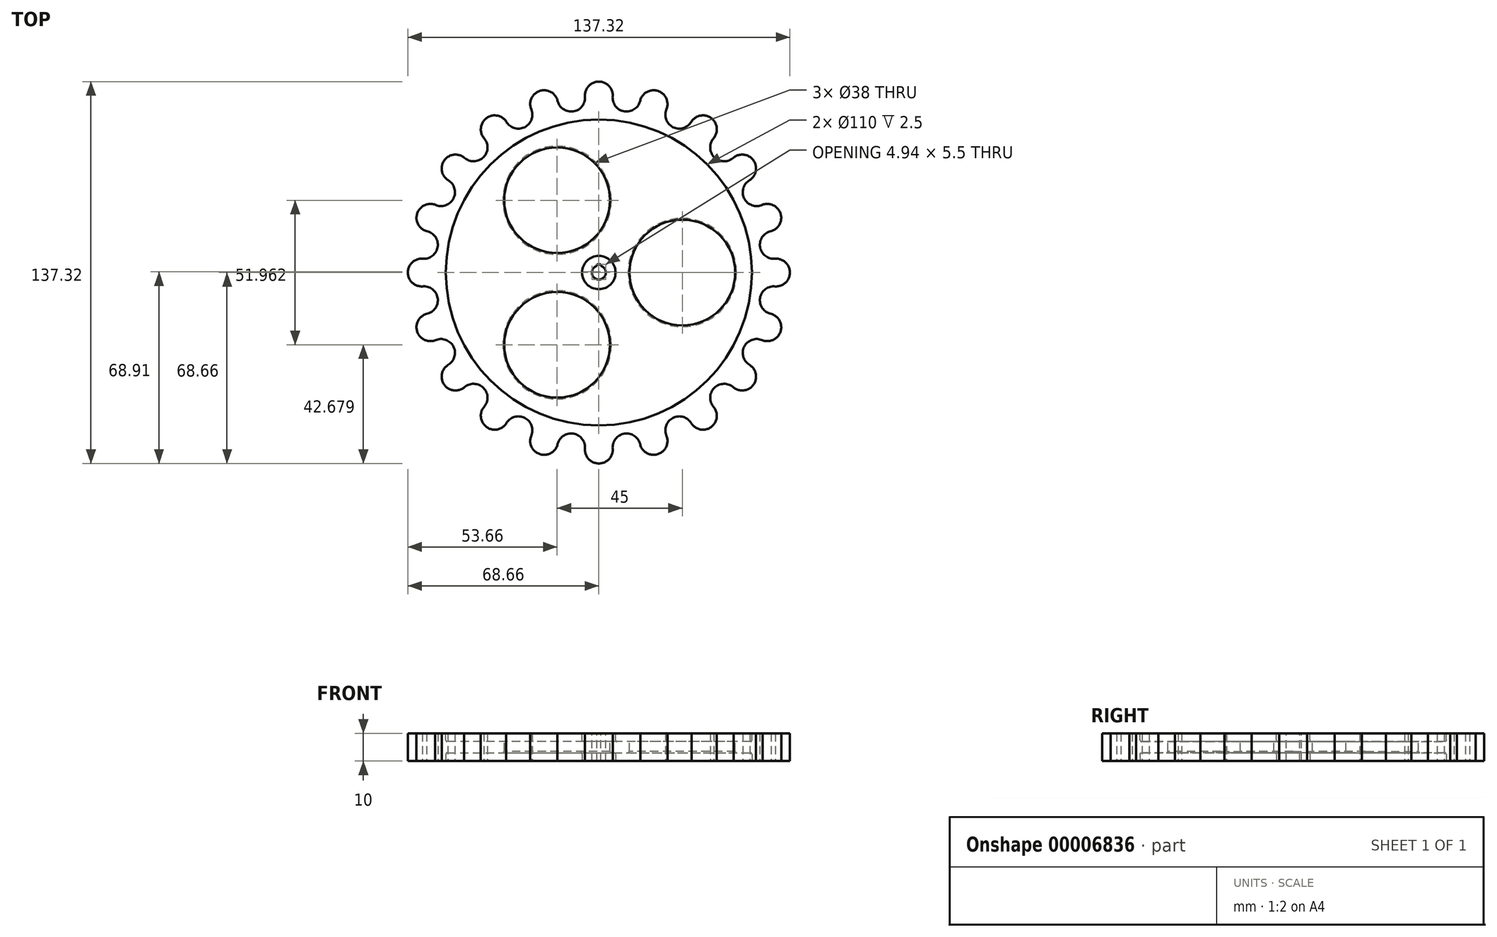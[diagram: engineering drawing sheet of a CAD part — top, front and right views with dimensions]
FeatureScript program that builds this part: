
annotation { "Feature Type Name" : "Feature", "Feature Type Description" : "" }
export const myFeature = defineFeature(function(context is Context, id is Id, definition is map)
    precondition{}
    {
        {
            var Q0;
            Q0=qCreatedBy(makeId("Top.planeOp"),FACE);
            var sketch = newSketch(context, id + "F0", { "sketchPlane" : qUnion([Q0])});
            skArc(sketch, "E0", {"start": v(4.96, 63.04) * mm, "mid": v(0, 68.66) * mm, "end": v(-4.96, 63.04) * mm});
            skCircle(sketch, "E1.1.0", {"center": v(-9.96, 62.88) * mm, "radius": 5 * mm});
            skArc(sketch, "E1.2.0", {"start": v(-14.76, 61.5) * mm, "mid": v(-21.22, 65.3) * mm, "end": v(-24.2, 58.43) * mm});
            skCircle(sketch, "E1.3.0", {"center": v(-28.9, 56.72) * mm, "radius": 5 * mm});
            skArc(sketch, "E1.4.0", {"start": v(-33.04, 53.92) * mm, "mid": v(-40.36, 55.55) * mm, "end": v(-41.07, 48.09) * mm});
            skCircle(sketch, "E1.5.0", {"center": v(-45.02, 45.02) * mm, "radius": 5 * mm});
            skArc(sketch, "E1.6.0", {"start": v(-48.09, 41.07) * mm, "mid": v(-55.55, 40.36) * mm, "end": v(-53.92, 33.04) * mm});
            skCircle(sketch, "E1.7.0", {"center": v(-56.72, 28.9) * mm, "radius": 5 * mm});
            skArc(sketch, "E1.8.0", {"start": v(-58.43, 24.2) * mm, "mid": v(-65.3, 21.22) * mm, "end": v(-61.5, 14.76) * mm});
            skCircle(sketch, "E1.9.0", {"center": v(-62.88, 9.96) * mm, "radius": 5 * mm});
            skArc(sketch, "E1.10.0", {"start": v(-63.04, 4.96) * mm, "mid": v(-68.66, 0) * mm, "end": v(-63.04, -4.96) * mm});
            skCircle(sketch, "E1.11.0", {"center": v(-62.88, -9.96) * mm, "radius": 5 * mm});
            skArc(sketch, "E1.12.0", {"start": v(-61.5, -14.76) * mm, "mid": v(-65.3, -21.22) * mm, "end": v(-58.43, -24.2) * mm});
            skCircle(sketch, "E1.13.0", {"center": v(-56.72, -28.9) * mm, "radius": 5 * mm});
            skArc(sketch, "E1.14.0", {"start": v(-53.92, -33.04) * mm, "mid": v(-55.55, -40.36) * mm, "end": v(-48.09, -41.07) * mm});
            skCircle(sketch, "E1.15.0", {"center": v(-45.02, -45.02) * mm, "radius": 5 * mm});
            skArc(sketch, "E1.16.0", {"start": v(-41.07, -48.09) * mm, "mid": v(-40.36, -55.55) * mm, "end": v(-33.04, -53.92) * mm});
            skCircle(sketch, "E1.17.0", {"center": v(-28.9, -56.72) * mm, "radius": 5 * mm});
            skArc(sketch, "E1.18.0", {"start": v(-24.2, -58.43) * mm, "mid": v(-21.22, -65.3) * mm, "end": v(-14.76, -61.5) * mm});
            skCircle(sketch, "E1.19.0", {"center": v(-9.96, -62.88) * mm, "radius": 5 * mm});
            skArc(sketch, "E1.20.0", {"start": v(-4.96, -63.04) * mm, "mid": v(0, -68.66) * mm, "end": v(4.96, -63.04) * mm});
            skCircle(sketch, "E1.21.0", {"center": v(9.96, -62.88) * mm, "radius": 5 * mm});
            skArc(sketch, "E1.22.0", {"start": v(14.76, -61.5) * mm, "mid": v(21.22, -65.3) * mm, "end": v(24.2, -58.43) * mm});
            skCircle(sketch, "E1.23.0", {"center": v(28.9, -56.72) * mm, "radius": 5 * mm});
            skArc(sketch, "E1.24.0", {"start": v(33.04, -53.92) * mm, "mid": v(40.36, -55.55) * mm, "end": v(41.07, -48.09) * mm});
            skCircle(sketch, "E1.25.0", {"center": v(45.02, -45.02) * mm, "radius": 5 * mm});
            skArc(sketch, "E1.26.0", {"start": v(48.09, -41.07) * mm, "mid": v(55.55, -40.36) * mm, "end": v(53.92, -33.04) * mm});
            skCircle(sketch, "E1.27.0", {"center": v(56.72, -28.9) * mm, "radius": 5 * mm});
            skArc(sketch, "E1.28.0", {"start": v(58.43, -24.2) * mm, "mid": v(65.3, -21.22) * mm, "end": v(61.5, -14.76) * mm});
            skCircle(sketch, "E1.29.0", {"center": v(62.88, -9.96) * mm, "radius": 5 * mm});
            skArc(sketch, "E1.30.0", {"start": v(63.04, -4.96) * mm, "mid": v(68.66, 0) * mm, "end": v(63.04, 4.96) * mm});
            skCircle(sketch, "E1.31.0", {"center": v(62.88, 9.96) * mm, "radius": 5 * mm});
            skArc(sketch, "E1.32.0", {"start": v(61.5, 14.76) * mm, "mid": v(65.3, 21.22) * mm, "end": v(58.43, 24.2) * mm});
            skCircle(sketch, "E1.33.0", {"center": v(56.72, 28.9) * mm, "radius": 5 * mm});
            skArc(sketch, "E1.34.0", {"start": v(53.92, 33.04) * mm, "mid": v(55.55, 40.36) * mm, "end": v(48.09, 41.07) * mm});
            skCircle(sketch, "E1.35.0", {"center": v(45.02, 45.02) * mm, "radius": 5 * mm});
            skArc(sketch, "E1.36.0", {"start": v(41.07, 48.09) * mm, "mid": v(40.36, 55.55) * mm, "end": v(33.04, 53.92) * mm});
            skCircle(sketch, "E1.37.0", {"center": v(28.9, 56.72) * mm, "radius": 5 * mm});
            skArc(sketch, "E1.38.0", {"start": v(24.2, 58.43) * mm, "mid": v(21.22, 65.3) * mm, "end": v(14.76, 61.5) * mm});
            skCircle(sketch, "E1.39.0", {"center": v(9.96, 62.88) * mm, "radius": 5 * mm});
            skPoint(sketch, "E1.center", {"position": v(0, 0) * mm});
            skSolve(sketch);
        }
        {
            var Q0;
            {var subQ0=sQuery(id+"F0.wireOp",EDGE,"E1.39.0");var subQ42=sQuery(id+"F0.wireOp",EDGE,"E0");var subQ81=makeQuery(id+"F0.imprint","INTERSECT",VERTEX,{"disambiguationData":[OD(1.0)],"derivedFrom":[subQ42,subQ0]});Q0=makeQuery(id+"F0.imprint","IMPRINT",FACE,{"disambiguationData":[TD([[makeQuery(id+"F0.imprint","IMPRINT",EDGE,{"disambiguationData":[TD([[subQ81,-1.0]])],"derivedFrom":subQ42}),1.0]])]});}
            extrude(context, id + "F1", {"entities" : qUnion([Q0]), "depth" : 10 * mm});
        }
        {
            var Q0;
            Q0=makeQuery(id+"F1.opExtrude","CAP_FACE",FACE,{"disambiguationData":[OSD([sQuery(id+"F0.wireOp",EDGE,"E0"),sQuery(id+"F0.wireOp",EDGE,"E1.1.0"),sQuery(id+"F0.wireOp",EDGE,"E1.2.0"),sQuery(id+"F0.wireOp",EDGE,"E1.3.0"),sQuery(id+"F0.wireOp",EDGE,"E1.4.0"),sQuery(id+"F0.wireOp",EDGE,"E1.5.0"),sQuery(id+"F0.wireOp",EDGE,"E1.6.0"),sQuery(id+"F0.wireOp",EDGE,"E1.7.0"),sQuery(id+"F0.wireOp",EDGE,"E1.8.0"),sQuery(id+"F0.wireOp",EDGE,"E1.9.0"),sQuery(id+"F0.wireOp",EDGE,"E1.10.0"),sQuery(id+"F0.wireOp",EDGE,"E1.11.0"),sQuery(id+"F0.wireOp",EDGE,"E1.12.0"),sQuery(id+"F0.wireOp",EDGE,"E1.13.0"),sQuery(id+"F0.wireOp",EDGE,"E1.14.0"),sQuery(id+"F0.wireOp",EDGE,"E1.15.0"),sQuery(id+"F0.wireOp",EDGE,"E1.16.0"),sQuery(id+"F0.wireOp",EDGE,"E1.17.0"),sQuery(id+"F0.wireOp",EDGE,"E1.18.0"),sQuery(id+"F0.wireOp",EDGE,"E1.19.0"),sQuery(id+"F0.wireOp",EDGE,"E1.20.0"),sQuery(id+"F0.wireOp",EDGE,"E1.21.0"),sQuery(id+"F0.wireOp",EDGE,"E1.22.0"),sQuery(id+"F0.wireOp",EDGE,"E1.23.0"),sQuery(id+"F0.wireOp",EDGE,"E1.24.0"),sQuery(id+"F0.wireOp",EDGE,"E1.25.0"),sQuery(id+"F0.wireOp",EDGE,"E1.26.0"),sQuery(id+"F0.wireOp",EDGE,"E1.27.0"),sQuery(id+"F0.wireOp",EDGE,"E1.28.0"),sQuery(id+"F0.wireOp",EDGE,"E1.29.0"),sQuery(id+"F0.wireOp",EDGE,"E1.30.0"),sQuery(id+"F0.wireOp",EDGE,"E1.31.0"),sQuery(id+"F0.wireOp",EDGE,"E1.32.0"),sQuery(id+"F0.wireOp",EDGE,"E1.33.0"),sQuery(id+"F0.wireOp",EDGE,"E1.34.0"),sQuery(id+"F0.wireOp",EDGE,"E1.35.0"),sQuery(id+"F0.wireOp",EDGE,"E1.36.0"),sQuery(id+"F0.wireOp",EDGE,"E1.37.0"),sQuery(id+"F0.wireOp",EDGE,"E1.38.0"),sQuery(id+"F0.wireOp",EDGE,"E1.39.0")])],"isStart":false});
            var sketch = newSketch(context, id + "F2", { "sketchPlane" : qUnion([Q0])});
            skArc(sketch, "E2", {"start": v(-0.75, 2.38) * mm, "mid": v(0, -2.5) * mm, "end": v(0.75, 2.38) * mm});
            skLineSegment(sketch, "E3", {"start": v(0, 3) * mm, "end": v(-0.75, 3) * mm});
            skLineSegment(sketch, "E4", {"start": v(-0.75, 3) * mm, "end": v(-0.75, 2.38) * mm});
            skLineSegment(sketch, "E5.0.MirrorCS", {"start": v(0, 3) * mm, "end": v(0.75, 3) * mm});
            skLineSegment(sketch, "E5.1.MirrorCS", {"start": v(0.75, 3) * mm, "end": v(0.75, 2.38) * mm});
            skSolve(sketch);
        }
        {
            var Q0;
            Q0=makeQuery(id+"F2.imprint","IMPRINT",FACE,{"disambiguationData":[TD([[makeQuery(id+"F2.imprint","IMPRINT",EDGE,{"derivedFrom":sQuery(id+"F2.wireOp",EDGE,"E2")}),1.0]])]});
            extrude(context, id + "F3", {"entities" : qUnion([Q0]), "operationType" : NewBodyOperationType.REMOVE, "endBound" : BoundingType.THROUGH_ALL, "oppositeDirection" : true, "depth" : 25 * mm});
        }
        {
            var Q0;
            Q0=makeQuery(id+"F1.opExtrude","CAP_FACE",FACE,{"disambiguationData":[OSD([sQuery(id+"F0.wireOp",EDGE,"E0"),sQuery(id+"F0.wireOp",EDGE,"E1.1.0"),sQuery(id+"F0.wireOp",EDGE,"E1.2.0"),sQuery(id+"F0.wireOp",EDGE,"E1.3.0"),sQuery(id+"F0.wireOp",EDGE,"E1.4.0"),sQuery(id+"F0.wireOp",EDGE,"E1.5.0"),sQuery(id+"F0.wireOp",EDGE,"E1.6.0"),sQuery(id+"F0.wireOp",EDGE,"E1.7.0"),sQuery(id+"F0.wireOp",EDGE,"E1.8.0"),sQuery(id+"F0.wireOp",EDGE,"E1.9.0"),sQuery(id+"F0.wireOp",EDGE,"E1.10.0"),sQuery(id+"F0.wireOp",EDGE,"E1.11.0"),sQuery(id+"F0.wireOp",EDGE,"E1.12.0"),sQuery(id+"F0.wireOp",EDGE,"E1.13.0"),sQuery(id+"F0.wireOp",EDGE,"E1.14.0"),sQuery(id+"F0.wireOp",EDGE,"E1.15.0"),sQuery(id+"F0.wireOp",EDGE,"E1.16.0"),sQuery(id+"F0.wireOp",EDGE,"E1.17.0"),sQuery(id+"F0.wireOp",EDGE,"E1.18.0"),sQuery(id+"F0.wireOp",EDGE,"E1.19.0"),sQuery(id+"F0.wireOp",EDGE,"E1.20.0"),sQuery(id+"F0.wireOp",EDGE,"E1.21.0"),sQuery(id+"F0.wireOp",EDGE,"E1.22.0"),sQuery(id+"F0.wireOp",EDGE,"E1.23.0"),sQuery(id+"F0.wireOp",EDGE,"E1.24.0"),sQuery(id+"F0.wireOp",EDGE,"E1.25.0"),sQuery(id+"F0.wireOp",EDGE,"E1.26.0"),sQuery(id+"F0.wireOp",EDGE,"E1.27.0"),sQuery(id+"F0.wireOp",EDGE,"E1.28.0"),sQuery(id+"F0.wireOp",EDGE,"E1.29.0"),sQuery(id+"F0.wireOp",EDGE,"E1.30.0"),sQuery(id+"F0.wireOp",EDGE,"E1.31.0"),sQuery(id+"F0.wireOp",EDGE,"E1.32.0"),sQuery(id+"F0.wireOp",EDGE,"E1.33.0"),sQuery(id+"F0.wireOp",EDGE,"E1.34.0"),sQuery(id+"F0.wireOp",EDGE,"E1.35.0"),sQuery(id+"F0.wireOp",EDGE,"E1.36.0"),sQuery(id+"F0.wireOp",EDGE,"E1.37.0"),sQuery(id+"F0.wireOp",EDGE,"E1.38.0"),sQuery(id+"F0.wireOp",EDGE,"E1.39.0")])],"isStart":false});
            var sketch = newSketch(context, id + "F4", { "sketchPlane" : qUnion([Q0])});
            skCircle(sketch, "E6", {"center": v(0, 0) * mm, "radius": 6 * mm});
            skCircle(sketch, "E7", {"center": v(0, 0) * mm, "radius": 55 * mm});
            skSolve(sketch);
        }
        {
            var Q0;
            Q0=makeQuery(id+"F4.imprint","IMPRINT",FACE,{"disambiguationData":[TD([[makeQuery(id+"F4.imprint","IMPRINT",EDGE,{"derivedFrom":sQuery(id+"F4.wireOp",EDGE,"E6")}),-1.0]])]});
            extrude(context, id + "F5", {"entities" : qUnion([Q0]), "operationType" : NewBodyOperationType.REMOVE, "oppositeDirection" : true, "depth" : 3 * mm});
        }
        {
            var Q0;
            Q0=makeQuery(id+"F1.opExtrude","CAP_FACE",FACE,{"disambiguationData":[OSD([sQuery(id+"F0.wireOp",EDGE,"E0"),sQuery(id+"F0.wireOp",EDGE,"E1.1.0"),sQuery(id+"F0.wireOp",EDGE,"E1.2.0"),sQuery(id+"F0.wireOp",EDGE,"E1.3.0"),sQuery(id+"F0.wireOp",EDGE,"E1.4.0"),sQuery(id+"F0.wireOp",EDGE,"E1.5.0"),sQuery(id+"F0.wireOp",EDGE,"E1.6.0"),sQuery(id+"F0.wireOp",EDGE,"E1.7.0"),sQuery(id+"F0.wireOp",EDGE,"E1.8.0"),sQuery(id+"F0.wireOp",EDGE,"E1.9.0"),sQuery(id+"F0.wireOp",EDGE,"E1.10.0"),sQuery(id+"F0.wireOp",EDGE,"E1.11.0"),sQuery(id+"F0.wireOp",EDGE,"E1.12.0"),sQuery(id+"F0.wireOp",EDGE,"E1.13.0"),sQuery(id+"F0.wireOp",EDGE,"E1.14.0"),sQuery(id+"F0.wireOp",EDGE,"E1.15.0"),sQuery(id+"F0.wireOp",EDGE,"E1.16.0"),sQuery(id+"F0.wireOp",EDGE,"E1.17.0"),sQuery(id+"F0.wireOp",EDGE,"E1.18.0"),sQuery(id+"F0.wireOp",EDGE,"E1.19.0"),sQuery(id+"F0.wireOp",EDGE,"E1.20.0"),sQuery(id+"F0.wireOp",EDGE,"E1.21.0"),sQuery(id+"F0.wireOp",EDGE,"E1.22.0"),sQuery(id+"F0.wireOp",EDGE,"E1.23.0"),sQuery(id+"F0.wireOp",EDGE,"E1.24.0"),sQuery(id+"F0.wireOp",EDGE,"E1.25.0"),sQuery(id+"F0.wireOp",EDGE,"E1.26.0"),sQuery(id+"F0.wireOp",EDGE,"E1.27.0"),sQuery(id+"F0.wireOp",EDGE,"E1.28.0"),sQuery(id+"F0.wireOp",EDGE,"E1.29.0"),sQuery(id+"F0.wireOp",EDGE,"E1.30.0"),sQuery(id+"F0.wireOp",EDGE,"E1.31.0"),sQuery(id+"F0.wireOp",EDGE,"E1.32.0"),sQuery(id+"F0.wireOp",EDGE,"E1.33.0"),sQuery(id+"F0.wireOp",EDGE,"E1.34.0"),sQuery(id+"F0.wireOp",EDGE,"E1.35.0"),sQuery(id+"F0.wireOp",EDGE,"E1.36.0"),sQuery(id+"F0.wireOp",EDGE,"E1.37.0"),sQuery(id+"F0.wireOp",EDGE,"E1.38.0"),sQuery(id+"F0.wireOp",EDGE,"E1.39.0")])],"isStart":true});
            var sketch = newSketch(context, id + "F6", { "sketchPlane" : qUnion([Q0])});
            skCircle(sketch, "E8", {"center": v(0, 0) * mm, "radius": 6 * mm});
            skCircle(sketch, "E9", {"center": v(0, 0) * mm, "radius": 55 * mm});
            skSolve(sketch);
        }
        {
            var Q0;
            Q0=makeQuery(id+"F6.imprint","IMPRINT",FACE,{"disambiguationData":[TD([[makeQuery(id+"F6.imprint","IMPRINT",EDGE,{"derivedFrom":sQuery(id+"F6.wireOp",EDGE,"E8")}),-1.0]])]});
            extrude(context, id + "F7", {"entities" : qUnion([Q0]), "operationType" : NewBodyOperationType.REMOVE, "oppositeDirection" : true, "depth" : 3 * mm});
        }
        {
            var Q0;
            Q0=makeQuery(id+"F5.boolean.opBoolean","COPY",FACE,{"derivedFrom":makeQuery(id+"F5.opExtrude","CAP_FACE",FACE,{"disambiguationData":[OSD([sQuery(id+"F4.wireOp",EDGE,"E6"),sQuery(id+"F4.wireOp",EDGE,"E7")])],"isStart":false})});
            var sketch = newSketch(context, id + "F8", { "sketchPlane" : qUnion([Q0])});
            skCircle(sketch, "E10", {"center": v(30, 0) * mm, "radius": 19 * mm});
            skCircle(sketch, "E11.1.0", {"center": v(-15, -25.98) * mm, "radius": 19 * mm});
            skCircle(sketch, "E11.2.0", {"center": v(-15, 25.98) * mm, "radius": 19 * mm});
            skPoint(sketch, "E11.center", {"position": v(0, 0) * mm});
            skLineSegment(sketch, "E11.anchor1", {"start": v(0, 0) * mm, "end": v(30, 0) * mm, "construction": true});
            skLineSegment(sketch, "E11.anchor2", {"start": v(0, 0) * mm, "end": v(-15, 25.98) * mm, "construction": true});
            skSolve(sketch);
        }
        {
            var Q0;
            Q0=makeQuery(id+"F8.imprint","IMPRINT",FACE,{"disambiguationData":[TD([[makeQuery(id+"F8.imprint","IMPRINT",EDGE,{"derivedFrom":sQuery(id+"F8.wireOp",EDGE,"E11.2.0")}),1.0]])]});
            var Q1;
            Q1=makeQuery(id+"F8.imprint","IMPRINT",FACE,{"disambiguationData":[TD([[makeQuery(id+"F8.imprint","IMPRINT",EDGE,{"derivedFrom":sQuery(id+"F8.wireOp",EDGE,"E11.1.0")}),1.0]])]});
            var Q2;
            Q2=makeQuery(id+"F8.imprint","IMPRINT",FACE,{"disambiguationData":[TD([[makeQuery(id+"F8.imprint","IMPRINT",EDGE,{"derivedFrom":sQuery(id+"F8.wireOp",EDGE,"E10")}),1.0]])]});
            extrude(context, id + "F9", {"entities" : qUnion([Q0, Q1, Q2]), "operationType" : NewBodyOperationType.REMOVE, "endBound" : BoundingType.THROUGH_ALL, "oppositeDirection" : true, "depth" : 25 * mm});
        }
        {
            var Q0;
            Q0=makeQuery(id+"F9.boolean.opBoolean","COPY",EDGE,{"derivedFrom":makeQuery(id+"F9.opExtrude","CAP_EDGE",EDGE,{"disambiguationData":[OSD([sQuery(id+"F8.wireOp",EDGE,"E11.1.0")])],"isStart":true})});
            var Q1;
            Q1=makeQuery(id+"F9.boolean.opBoolean","INTERSECT",EDGE,{"derivedFrom":[makeQuery(id+"F7.boolean.opBoolean","COPY",FACE,{"derivedFrom":makeQuery(id+"F7.opExtrude","CAP_FACE",FACE,{"disambiguationData":[OSD([sQuery(id+"F6.wireOp",EDGE,"E8"),sQuery(id+"F6.wireOp",EDGE,"E9")])],"isStart":false})}),makeQuery(id+"F9.opExtrude","SWEPT_FACE",FACE,{"disambiguationData":[OSD([sQuery(id+"F8.wireOp",EDGE,"E11.1.0")])]})]});
            var Q2;
            Q2=makeQuery(id+"F9.boolean.opBoolean","INTERSECT",EDGE,{"derivedFrom":[makeQuery(id+"F7.boolean.opBoolean","COPY",FACE,{"derivedFrom":makeQuery(id+"F7.opExtrude","CAP_FACE",FACE,{"disambiguationData":[OSD([sQuery(id+"F6.wireOp",EDGE,"E8"),sQuery(id+"F6.wireOp",EDGE,"E9")])],"isStart":false})}),makeQuery(id+"F9.opExtrude","SWEPT_FACE",FACE,{"disambiguationData":[OSD([sQuery(id+"F8.wireOp",EDGE,"E11.2.0")])]})]});
            var Q3;
            Q3=makeQuery(id+"F9.boolean.opBoolean","COPY",EDGE,{"derivedFrom":makeQuery(id+"F9.opExtrude","CAP_EDGE",EDGE,{"disambiguationData":[OSD([sQuery(id+"F8.wireOp",EDGE,"E11.2.0")])],"isStart":true})});
            var Q4;
            Q4=makeQuery(id+"F9.boolean.opBoolean","INTERSECT",EDGE,{"derivedFrom":[makeQuery(id+"F7.boolean.opBoolean","COPY",FACE,{"derivedFrom":makeQuery(id+"F7.opExtrude","CAP_FACE",FACE,{"disambiguationData":[OSD([sQuery(id+"F6.wireOp",EDGE,"E8"),sQuery(id+"F6.wireOp",EDGE,"E9")])],"isStart":false})}),makeQuery(id+"F9.opExtrude","SWEPT_FACE",FACE,{"disambiguationData":[OSD([sQuery(id+"F8.wireOp",EDGE,"E10")])]})]});
            var Q5;
            Q5=makeQuery(id+"F9.boolean.opBoolean","COPY",EDGE,{"derivedFrom":makeQuery(id+"F9.opExtrude","CAP_EDGE",EDGE,{"disambiguationData":[OSD([sQuery(id+"F8.wireOp",EDGE,"E10")])],"isStart":true})});
            var Q6;
            Q6=makeQuery(id+"F5.boolean.opBoolean","COPY",EDGE,{"derivedFrom":makeQuery(id+"F5.opExtrude","CAP_EDGE",EDGE,{"disambiguationData":[OSD([sQuery(id+"F4.wireOp",EDGE,"E7")])],"isStart":true})});
            var Q7;
            Q7=makeQuery(id+"F7.boolean.opBoolean","COPY",EDGE,{"derivedFrom":makeQuery(id+"F7.opExtrude","CAP_EDGE",EDGE,{"disambiguationData":[OSD([sQuery(id+"F6.wireOp",EDGE,"E9")])],"isStart":true})});
            chamfer(context, id + "F10", {"entities" : qUnion([Q0, Q1, Q2, Q3, Q4, Q5, Q6, Q7]), "width" : .5 * mm, "tangentPropagation" : true});
        }
        {
            var Q0;
            Q0=makeQuery(id+"F7.boolean.opBoolean","COPY",EDGE,{"derivedFrom":makeQuery(id+"F7.opExtrude","CAP_EDGE",EDGE,{"disambiguationData":[OSD([sQuery(id+"F6.wireOp",EDGE,"E9")])],"isStart":false})});
            var Q1;
            Q1=makeQuery(id+"F7.boolean.opBoolean","COPY",EDGE,{"derivedFrom":makeQuery(id+"F7.opExtrude","CAP_EDGE",EDGE,{"disambiguationData":[OSD([sQuery(id+"F6.wireOp",EDGE,"E8")])],"isStart":false})});
            var Q2;
            Q2=makeQuery(id+"F5.boolean.opBoolean","COPY",EDGE,{"derivedFrom":makeQuery(id+"F5.opExtrude","CAP_EDGE",EDGE,{"disambiguationData":[OSD([sQuery(id+"F4.wireOp",EDGE,"E7")])],"isStart":false})});
            var Q3;
            Q3=makeQuery(id+"F5.boolean.opBoolean","COPY",EDGE,{"derivedFrom":makeQuery(id+"F5.opExtrude","CAP_EDGE",EDGE,{"disambiguationData":[OSD([sQuery(id+"F4.wireOp",EDGE,"E6")])],"isStart":false})});
            fillet(context, id + "F11", {"entities" : qUnion([Q0, Q1, Q2, Q3]), "radius" : .5 * mm, "tangentPropagation" : true, "allowEdgeOverflow" : false});
        }
        {
            var Q0;
            Q0=makeQuery(id+"F1.opExtrude","SWEPT_BODY",BODY,{"disambiguationData":[OSD([sQuery(id+"F0.wireOp",EDGE,"E0"),sQuery(id+"F0.wireOp",EDGE,"E1.1.0"),sQuery(id+"F0.wireOp",EDGE,"E1.2.0"),sQuery(id+"F0.wireOp",EDGE,"E1.3.0"),sQuery(id+"F0.wireOp",EDGE,"E1.4.0"),sQuery(id+"F0.wireOp",EDGE,"E1.5.0"),sQuery(id+"F0.wireOp",EDGE,"E1.6.0"),sQuery(id+"F0.wireOp",EDGE,"E1.7.0"),sQuery(id+"F0.wireOp",EDGE,"E1.8.0"),sQuery(id+"F0.wireOp",EDGE,"E1.9.0"),sQuery(id+"F0.wireOp",EDGE,"E1.10.0"),sQuery(id+"F0.wireOp",EDGE,"E1.11.0"),sQuery(id+"F0.wireOp",EDGE,"E1.12.0"),sQuery(id+"F0.wireOp",EDGE,"E1.13.0"),sQuery(id+"F0.wireOp",EDGE,"E1.14.0"),sQuery(id+"F0.wireOp",EDGE,"E1.15.0"),sQuery(id+"F0.wireOp",EDGE,"E1.16.0"),sQuery(id+"F0.wireOp",EDGE,"E1.17.0"),sQuery(id+"F0.wireOp",EDGE,"E1.18.0"),sQuery(id+"F0.wireOp",EDGE,"E1.19.0"),sQuery(id+"F0.wireOp",EDGE,"E1.20.0"),sQuery(id+"F0.wireOp",EDGE,"E1.21.0"),sQuery(id+"F0.wireOp",EDGE,"E1.22.0"),sQuery(id+"F0.wireOp",EDGE,"E1.23.0"),sQuery(id+"F0.wireOp",EDGE,"E1.24.0"),sQuery(id+"F0.wireOp",EDGE,"E1.25.0"),sQuery(id+"F0.wireOp",EDGE,"E1.26.0"),sQuery(id+"F0.wireOp",EDGE,"E1.27.0"),sQuery(id+"F0.wireOp",EDGE,"E1.28.0"),sQuery(id+"F0.wireOp",EDGE,"E1.29.0"),sQuery(id+"F0.wireOp",EDGE,"E1.30.0"),sQuery(id+"F0.wireOp",EDGE,"E1.31.0"),sQuery(id+"F0.wireOp",EDGE,"E1.32.0"),sQuery(id+"F0.wireOp",EDGE,"E1.33.0"),sQuery(id+"F0.wireOp",EDGE,"E1.34.0"),sQuery(id+"F0.wireOp",EDGE,"E1.35.0"),sQuery(id+"F0.wireOp",EDGE,"E1.36.0"),sQuery(id+"F0.wireOp",EDGE,"E1.37.0"),sQuery(id+"F0.wireOp",EDGE,"E1.38.0"),sQuery(id+"F0.wireOp",EDGE,"E1.39.0")])]});
            transform(context, id + "F12", {"entities" : qUnion([Q0]), "transformType" : TransformType.TRANSLATION_3D, "dx" : 0 * mm, "dy" : 200 * mm, "dz" : 0 * mm, "makeCopy" : true});
        }
        {
            var Q0;
            Q0=makeQuery(id+"F12.opPattern","COPY",BODY,{"derivedFrom":makeQuery(id+"F1.opExtrude","SWEPT_BODY",BODY,{"disambiguationData":[OSD([sQuery(id+"F0.wireOp",EDGE,"E0"),sQuery(id+"F0.wireOp",EDGE,"E1.1.0"),sQuery(id+"F0.wireOp",EDGE,"E1.2.0"),sQuery(id+"F0.wireOp",EDGE,"E1.3.0"),sQuery(id+"F0.wireOp",EDGE,"E1.4.0"),sQuery(id+"F0.wireOp",EDGE,"E1.5.0"),sQuery(id+"F0.wireOp",EDGE,"E1.6.0"),sQuery(id+"F0.wireOp",EDGE,"E1.7.0"),sQuery(id+"F0.wireOp",EDGE,"E1.8.0"),sQuery(id+"F0.wireOp",EDGE,"E1.9.0"),sQuery(id+"F0.wireOp",EDGE,"E1.10.0"),sQuery(id+"F0.wireOp",EDGE,"E1.11.0"),sQuery(id+"F0.wireOp",EDGE,"E1.12.0"),sQuery(id+"F0.wireOp",EDGE,"E1.13.0"),sQuery(id+"F0.wireOp",EDGE,"E1.14.0"),sQuery(id+"F0.wireOp",EDGE,"E1.15.0"),sQuery(id+"F0.wireOp",EDGE,"E1.16.0"),sQuery(id+"F0.wireOp",EDGE,"E1.17.0"),sQuery(id+"F0.wireOp",EDGE,"E1.18.0"),sQuery(id+"F0.wireOp",EDGE,"E1.19.0"),sQuery(id+"F0.wireOp",EDGE,"E1.20.0"),sQuery(id+"F0.wireOp",EDGE,"E1.21.0"),sQuery(id+"F0.wireOp",EDGE,"E1.22.0"),sQuery(id+"F0.wireOp",EDGE,"E1.23.0"),sQuery(id+"F0.wireOp",EDGE,"E1.24.0"),sQuery(id+"F0.wireOp",EDGE,"E1.25.0"),sQuery(id+"F0.wireOp",EDGE,"E1.26.0"),sQuery(id+"F0.wireOp",EDGE,"E1.27.0"),sQuery(id+"F0.wireOp",EDGE,"E1.28.0"),sQuery(id+"F0.wireOp",EDGE,"E1.29.0"),sQuery(id+"F0.wireOp",EDGE,"E1.30.0"),sQuery(id+"F0.wireOp",EDGE,"E1.31.0"),sQuery(id+"F0.wireOp",EDGE,"E1.32.0"),sQuery(id+"F0.wireOp",EDGE,"E1.33.0"),sQuery(id+"F0.wireOp",EDGE,"E1.34.0"),sQuery(id+"F0.wireOp",EDGE,"E1.35.0"),sQuery(id+"F0.wireOp",EDGE,"E1.36.0"),sQuery(id+"F0.wireOp",EDGE,"E1.37.0"),sQuery(id+"F0.wireOp",EDGE,"E1.38.0"),sQuery(id+"F0.wireOp",EDGE,"E1.39.0")])]}),"instanceName":"1"});
            deleteBodies(context, id + "F13", {"entities" : qUnion([Q0])});
        }
    });
